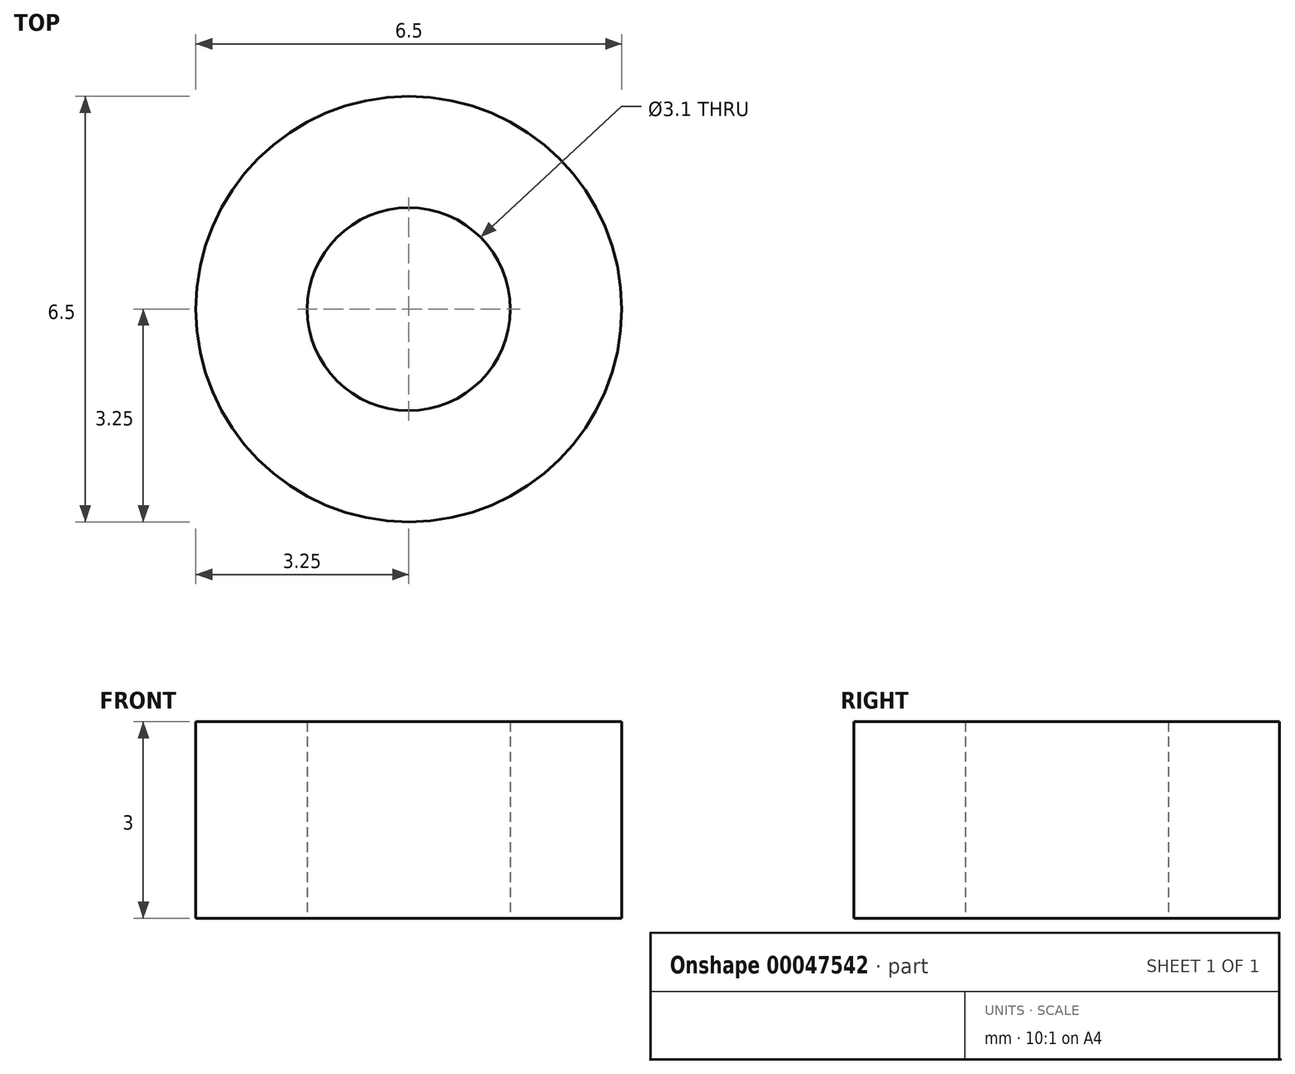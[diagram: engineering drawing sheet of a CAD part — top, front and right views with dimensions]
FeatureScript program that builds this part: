
annotation { "Feature Type Name" : "Feature", "Feature Type Description" : "" }
export const myFeature = defineFeature(function(context is Context, id is Id, definition is map)
    precondition{}
    {
        {
            var Q0;
            Q0=qCreatedBy(makeId("Top.planeOp"),FACE);
            var sketch = newSketch(context, id + "F0", { "sketchPlane" : qUnion([Q0])});
            skCircle(sketch, "E0", {"center": v(0, 0) * mm, "radius": 3.25 * mm});
            skCircle(sketch, "E1", {"center": v(0, 0) * mm, "radius": 1.55 * mm});
            skSolve(sketch);
        }
        {
            var Q0;
            Q0 = qSketchRegion(id + "F0", true);
            extrude(context, id + "F1", {"entities" : qUnion([Q0]), "depth" : 3 * mm});
        }
    });
